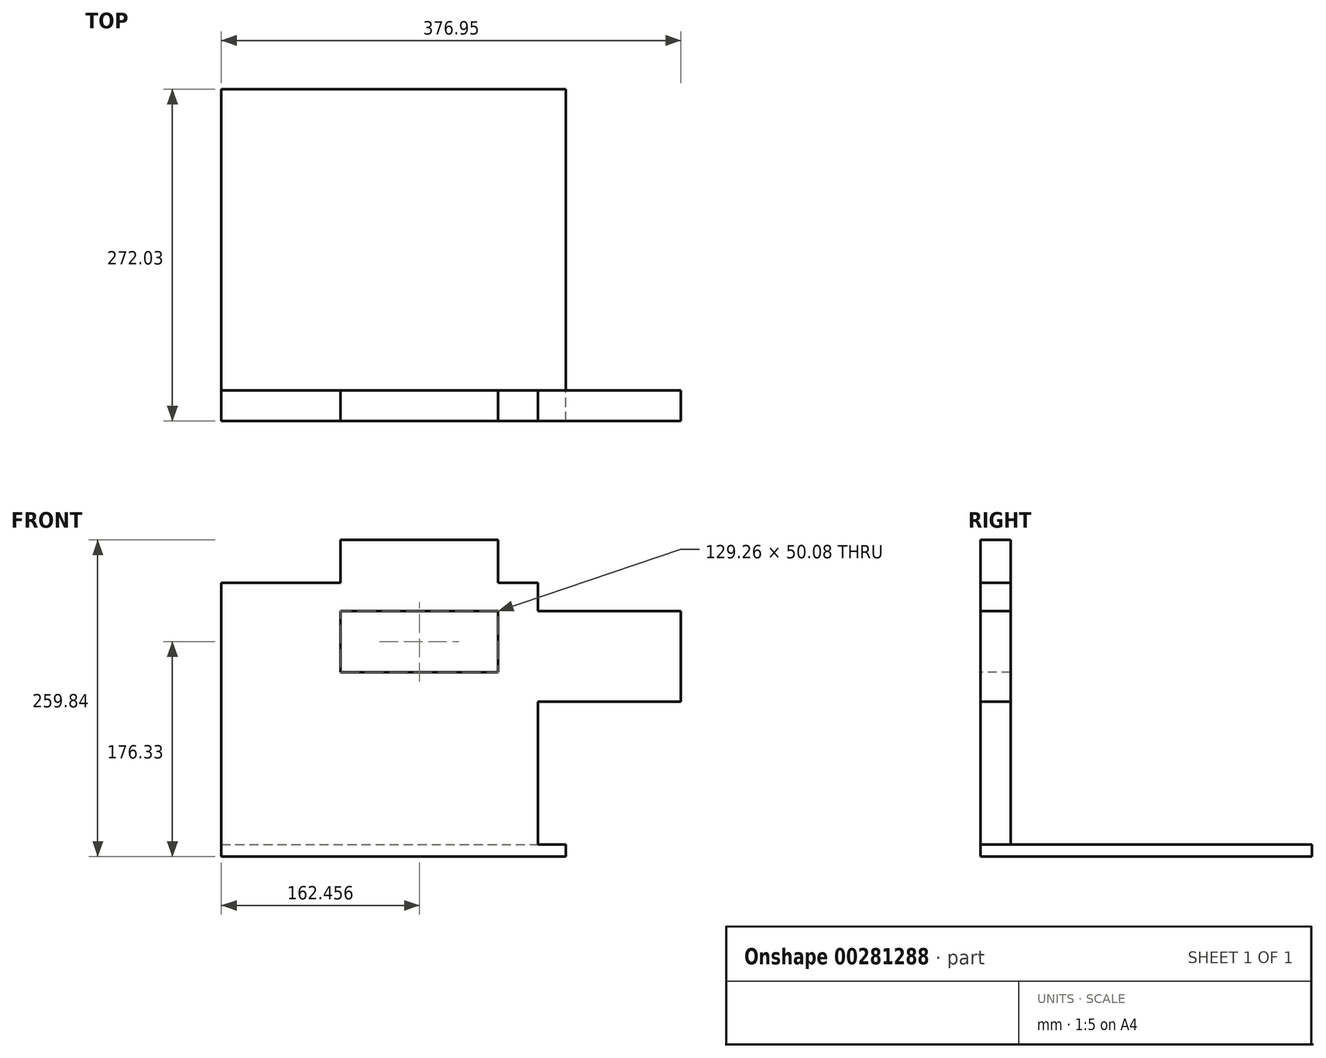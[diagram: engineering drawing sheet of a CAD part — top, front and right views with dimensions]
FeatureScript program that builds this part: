
annotation { "Feature Type Name" : "Feature", "Feature Type Description" : "" }
export const myFeature = defineFeature(function(context is Context, id is Id, definition is map)
    precondition{}
    {
        {
            var Q0;
            Q0=qCreatedBy(makeId("Top.planeOp"),FACE);
            var sketch = newSketch(context, id + "F0", { "sketchPlane" : qUnion([Q0])});
            skLineSegment(sketch, "E0.bottom", {"start": v(0, 0) * mm, "end": v(282.45, 0) * mm});
            skLineSegment(sketch, "E0.top", {"start": v(0, 272.03) * mm, "end": v(282.45, 272.03) * mm});
            skLineSegment(sketch, "E0.left", {"start": v(0, 0) * mm, "end": v(0, 272.03) * mm});
            skLineSegment(sketch, "E0.right", {"start": v(282.45, 0) * mm, "end": v(282.45, 272.03) * mm});
            skSolve(sketch);
        }
        {
            var Q0;
            Q0=makeQuery(id+"F0.imprint","IMPRINT",FACE,{"disambiguationData":[TD([[makeQuery(id+"F0.imprint","IMPRINT",EDGE,{"derivedFrom":sQuery(id+"F0.wireOp",EDGE,"E0.bottom")}),1.0]])]});
            extrude(context, id + "F1", {"entities" : qUnion([Q0]), "depth" : 10 * mm});
        }
        {
            var Q0;
            Q0=qCreatedBy(makeId("Front.planeOp"),FACE);
            var sketch = newSketch(context, id + "F2", { "sketchPlane" : qUnion([Q0])});
            skLineSegment(sketch, "E1.bottom", {"start": v(0, 0) * mm, "end": v(259.5, 0) * mm});
            skLineSegment(sketch, "E1.top", {"start": v(0, 224.5) * mm, "end": v(259.5, 224.5) * mm});
            skLineSegment(sketch, "E1.left", {"start": v(0, 0) * mm, "end": v(0, 224.5) * mm});
            skLineSegment(sketch, "E1.right", {"start": v(259.5, 0) * mm, "end": v(259.5, 224.5) * mm});
            skLineSegment(sketch, "E2.bottom", {"start": v(91.92, 201.37) * mm, "end": v(376.95, 201.37) * mm});
            skLineSegment(sketch, "E2.top", {"start": v(91.92, 127.14) * mm, "end": v(376.95, 127.14) * mm});
            skLineSegment(sketch, "E2.left", {"start": v(91.92, 201.37) * mm, "end": v(91.92, 127.14) * mm});
            skLineSegment(sketch, "E2.right", {"start": v(376.95, 201.37) * mm, "end": v(376.95, 127.14) * mm});
            skLineSegment(sketch, "E3.bottom", {"start": v(97.82, 259.84) * mm, "end": v(227.09, 259.84) * mm});
            skLineSegment(sketch, "E3.top", {"start": v(97.82, 151.3) * mm, "end": v(227.09, 151.3) * mm});
            skLineSegment(sketch, "E3.left", {"start": v(97.82, 259.84) * mm, "end": v(97.82, 151.3) * mm});
            skLineSegment(sketch, "E3.right", {"start": v(227.09, 259.84) * mm, "end": v(227.09, 151.3) * mm});
            skSolve(sketch);
        }
        {
            var Q0;
            Q0=makeQuery(id+"F2.imprint","IMPRINT",FACE,{"disambiguationData":[TD([[makeQuery(id+"F2.imprint","IMPRINT",EDGE,{"derivedFrom":sQuery(id+"F2.wireOp",EDGE,"E1.bottom")}),1.0]])]});
            var Q1;
            {var subQ5=sQuery(id+"F2.wireOp",EDGE,"E2.right");Q1=makeQuery(id+"F2.imprint","IMPRINT",FACE,{"disambiguationData":[TD([[makeQuery(id+"F2.imprint","IMPRINT",EDGE,{"derivedFrom":subQ5}),-1.0]])]});}
            var Q2;
            {var subQ5=sQuery(id+"F2.wireOp",EDGE,"E3.bottom");Q2=makeQuery(id+"F2.imprint","IMPRINT",FACE,{"disambiguationData":[TD([[makeQuery(id+"F2.imprint","IMPRINT",EDGE,{"derivedFrom":subQ5}),-1.0]])]});}
            var Q3;
            {var subQ0=sQuery(id+"F2.wireOp",EDGE,"E1.right");var subQ1=sQuery(id+"F2.wireOp",EDGE,"E1.top");var subQ2=makeQuery(id+"F2.imprint","INTERSECT",VERTEX,{"derivedFrom":[subQ1,subQ0]});Q3=makeQuery(id+"F2.imprint","IMPRINT",FACE,{"disambiguationData":[TD([[makeQuery(id+"F2.imprint","IMPRINT",EDGE,{"disambiguationData":[TD([[subQ2,1.0]])],"derivedFrom":subQ1}),-1.0]])]});}
            var Q4;
            {var subQ0=sQuery(id+"F2.wireOp",EDGE,"E3.left");var subQ1=sQuery(id+"F2.wireOp",EDGE,"E1.top");var subQ2=makeQuery(id+"F2.imprint","INTERSECT",VERTEX,{"derivedFrom":[subQ1,subQ0]});Q4=makeQuery(id+"F2.imprint","IMPRINT",FACE,{"disambiguationData":[TD([[makeQuery(id+"F2.imprint","IMPRINT",EDGE,{"disambiguationData":[TD([[subQ2,-1.0]])],"derivedFrom":subQ1}),-1.0]])]});}
            var Q5;
            {var subQ0=sQuery(id+"F2.wireOp",EDGE,"E2.left");Q5=makeQuery(id+"F2.imprint","IMPRINT",FACE,{"disambiguationData":[TD([[makeQuery(id+"F2.imprint","IMPRINT",EDGE,{"derivedFrom":subQ0}),1.0]])]});}
            extrude(context, id + "F3", {"entities" : qUnion([Q0, Q1, Q2, Q3, Q4, Q5]), "operationType" : NewBodyOperationType.ADD, "oppositeDirection" : true, "depth" : 25 * mm});
        }
    });
